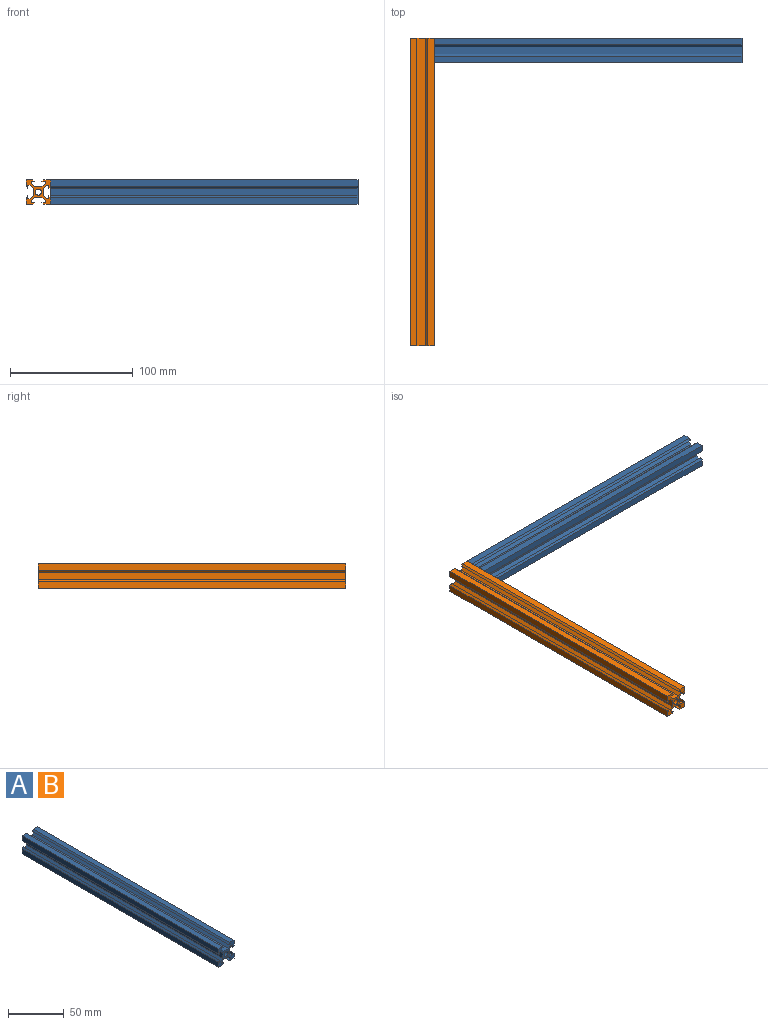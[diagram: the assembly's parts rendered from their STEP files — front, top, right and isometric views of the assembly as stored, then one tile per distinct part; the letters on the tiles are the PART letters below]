
ASSEMBLY  parts=2 mates=1
PART A: 47 faces, bbox 20x250x20 mm
  f0: plane 250x5.5mm, normal (0,0,1), area 1375mm2, adj f1,f8,f9,f11
  f1: plane 250x5.5mm, normal (-1,0,0), area 1375mm2, adj f0,f8,f9,f30
  f2: plane 250x5.5mm, normal (0,0,-1), area 1375mm2, adj f5,f8,f9,f21
  f3: plane 250x5.5mm, normal (1,0,0), area 1375mm2, adj f4,f8,f9,f38
  f4: plane 250x5.5mm, normal (0,0,1), area 1375mm2, adj f3,f8,f9,f12
  f5: plane 250x5.5mm, normal (-1,0,0), area 1375mm2, adj f2,f8,f9,f29
  f6: plane 250x5.5mm, normal (0,0,-1), area 1375mm2, adj f7,f8,f9,f20
  f7: plane 250x5.5mm, normal (1,0,0), area 1375mm2, adj f6,f8,f9,f39
  f8: plane 20x20mm, normal (0,1,0), area 171.2mm2, adj f0,f1,f2,f3,f4,f5,f6,f7
  f9: plane 20x20mm, normal (0,-1,0), area 171.2mm2, adj f0,f1,f2,f3,f4,f5,f6,f7
  f10: cylinder r=2.5mm len=250mm, axis (0,-1,0), area 3927mm2, adj f8,f9
  f11: plane 250x1.5mm, normal (0.71,0,0.71), area 530.3mm2, adj f0,f8,f9,f13
  f12: plane 250x1.5mm, normal (-0.71,0,0.71), area 530.3mm2, adj f4,f8,f9,f19
  f13: plane 250x2.5mm, normal (0,0,-1), area 625mm2, adj f8,f9,f11,f14
  f14: plane 250x1.8mm, normal (1,0,0), area 450mm2, adj f8,f9,f13,f15
  f15: plane 250x2.5mm, normal (0.71,0,0.71), area 883.9mm2, adj f8,f9,f14,f16
  f16: plane 250x6mm, normal (0,0,1), area 1500mm2, adj f8,f9,f15,f17
  f17: plane 250x2.5mm, normal (-0.71,0,0.71), area 883.9mm2, adj f8,f9,f16,f18
  f18: plane 250x1.8mm, normal (-1,0,0), area 450mm2, adj f8,f9,f17,f19
  f19: plane 250x2.5mm, normal (0,0,-1), area 625mm2, adj f8,f9,f12,f18
  f20: plane 250x1.5mm, normal (-0.71,0,-0.71), area 530.3mm2, adj f6,f8,f9,f22
  f21: plane 250x1.5mm, normal (0.71,0,-0.71), area 530.3mm2, adj f2,f8,f9,f28
  f22: plane 250x2.5mm, normal (0,0,1), area 625mm2, adj f8,f9,f20,f23
  f23: plane 250x1.8mm, normal (-1,0,0), area 450mm2, adj f8,f9,f22,f24
  f24: plane 250x2.5mm, normal (-0.71,0,-0.71), area 883.9mm2, adj f8,f9,f23,f25
  f25: plane 250x6mm, normal (0,0,-1), area 1500mm2, adj f8,f9,f24,f26
  f26: plane 250x2.5mm, normal (0.71,0,-0.71), area 883.9mm2, adj f8,f9,f25,f27
  f27: plane 250x1.8mm, normal (1,0,0), area 450mm2, adj f8,f9,f26,f28
  f28: plane 250x2.5mm, normal (0,0,1), area 625mm2, adj f8,f9,f21,f27
  f29: plane 250x1.5mm, normal (-0.71,0,0.71), area 530.3mm2, adj f5,f8,f9,f31
  f30: plane 250x1.5mm, normal (-0.71,0,-0.71), area 530.3mm2, adj f1,f8,f9,f37
  f31: plane 250x2.5mm, normal (1,0,0), area 625mm2, adj f8,f9,f29,f32
  f32: plane 250x1.8mm, normal (0,0,1), area 450mm2, adj f8,f9,f31,f33
  f33: plane 250x2.5mm, normal (-0.71,0,0.71), area 883.9mm2, adj f8,f9,f32,f34
  f34: plane 250x6mm, normal (-1,0,0), area 1500mm2, adj f8,f9,f33,f35
  f35: plane 250x2.5mm, normal (-0.71,0,-0.71), area 883.9mm2, adj f8,f9,f34,f36
  f36: plane 250x1.8mm, normal (0,0,-1), area 450mm2, adj f8,f9,f35,f37
  f37: plane 250x2.5mm, normal (1,0,0), area 625mm2, adj f8,f9,f30,f36
  f38: plane 250x1.5mm, normal (0.71,0,-0.71), area 530.3mm2, adj f3,f8,f9,f40
  f39: plane 250x1.5mm, normal (0.71,0,0.71), area 530.3mm2, adj f7,f8,f9,f46
  f40: plane 250x2.5mm, normal (-1,0,0), area 625mm2, adj f8,f9,f38,f41
  f41: plane 250x1.8mm, normal (0,0,-1), area 450mm2, adj f8,f9,f40,f42
  f42: plane 250x2.5mm, normal (0.71,0,-0.71), area 883.9mm2, adj f8,f9,f41,f43
  f43: plane 250x6mm, normal (1,0,0), area 1500mm2, adj f8,f9,f42,f44
  f44: plane 250x2.5mm, normal (0.71,0,0.71), area 883.9mm2, adj f8,f9,f43,f45
  f45: plane 250x1.8mm, normal (0,0,1), area 450mm2, adj f8,f9,f44,f46
  f46: plane 250x2.5mm, normal (-1,0,0), area 625mm2, adj f8,f9,f39,f45
PART B: same geometry as A
PLACE A rot(axis=(0,0,-1),90deg) t=(-37.3,115.1,-80.8)mm
PLACE B t=(-47.3,-125,-80.95)mm
MATE planar B.f3 <-> A.f10  axis (1,0,0) through (-37.3,125,-73.7)mm
